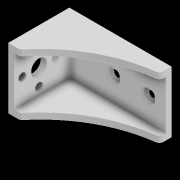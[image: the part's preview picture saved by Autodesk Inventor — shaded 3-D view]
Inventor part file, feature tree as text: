
AUTODESK INVENTOR PART (.ipt)
format: ipt  version: 2020 (Build 240168000, 168)  size: 202,752 bytes
history: native  units: mm
features: sketch x6, extrude x4, fillet x2, hole x2, pattern_circular x1
ambient origin geometry x8: Origin, YZ Plane, XZ Plane, XY Plane, X Axis, Y Axis, Z Axis, Center Point
bodies: Solid1 (feature_tree)
feature tree (15):
  extrude  "Extrusion1"  Depth=31.0mm
  extrude  "Extrusion2"  Depth=6.0mm
  fillet  "Fillet1"  Radius=2.0mm
  hole  "Hole1"  [1 undecoded]
  hole  "Hole2"  [1 undecoded]
  pattern_circular  "Circular Pattern1"  [2 undecoded]
  extrude  "Extrusion4"  Depth=2.0mm TaperAngle=360.0deg
  extrude  "Extrusion5"  Depth=12.5mm
  fillet  "Fillet2"  Radius=3.0mm
  sketch  "Sketch1"  dims[d0=52.0mm d1=31.0mm]
  sketch  "Sketch2"  dims[d2=6.0mm d3=6.0mm d4=2.0mm]
  sketch  "Sketch4"  dims[d5=22.7mm d6=6.0mm d7=6.0mm d8=2.0mm d9=5.458mm]
  sketch  "Sketch5"  dims[d10=3.0mm d11=0.0mm d12=3.0mm]
  sketch  "Sketch7"  dims[d13=28.0mm d14=0.0mm]
  sketch  "Sketch8"  dims[d19=2.0mm d20=8.0mm d21=6.0mm d22=4.0mm d23=2.0mm d24=90.0deg d25=8.0mm d26=0.0mm d28=8.5mm d29=3.74mm d30=6.0mm d31=4.0mm d32=2.0mm d33=90.0deg d34=8.0mm d35=0.0mm d36=40.0mm d37=360.0deg d40=12.5mm d41=3.0mm d42=3.0mm d43=10.0mm d44=0.0mm d45=3.0mm d46=3.0mm d47=67.470785mm d48=10.0mm d49=0.0mm d50=2.0mm]
note: 4 required parameter values undecoded (feature->parameter linkage not recoverable at this tier; creation-order binding heuristic only, values carry confidence <= 0.55)
